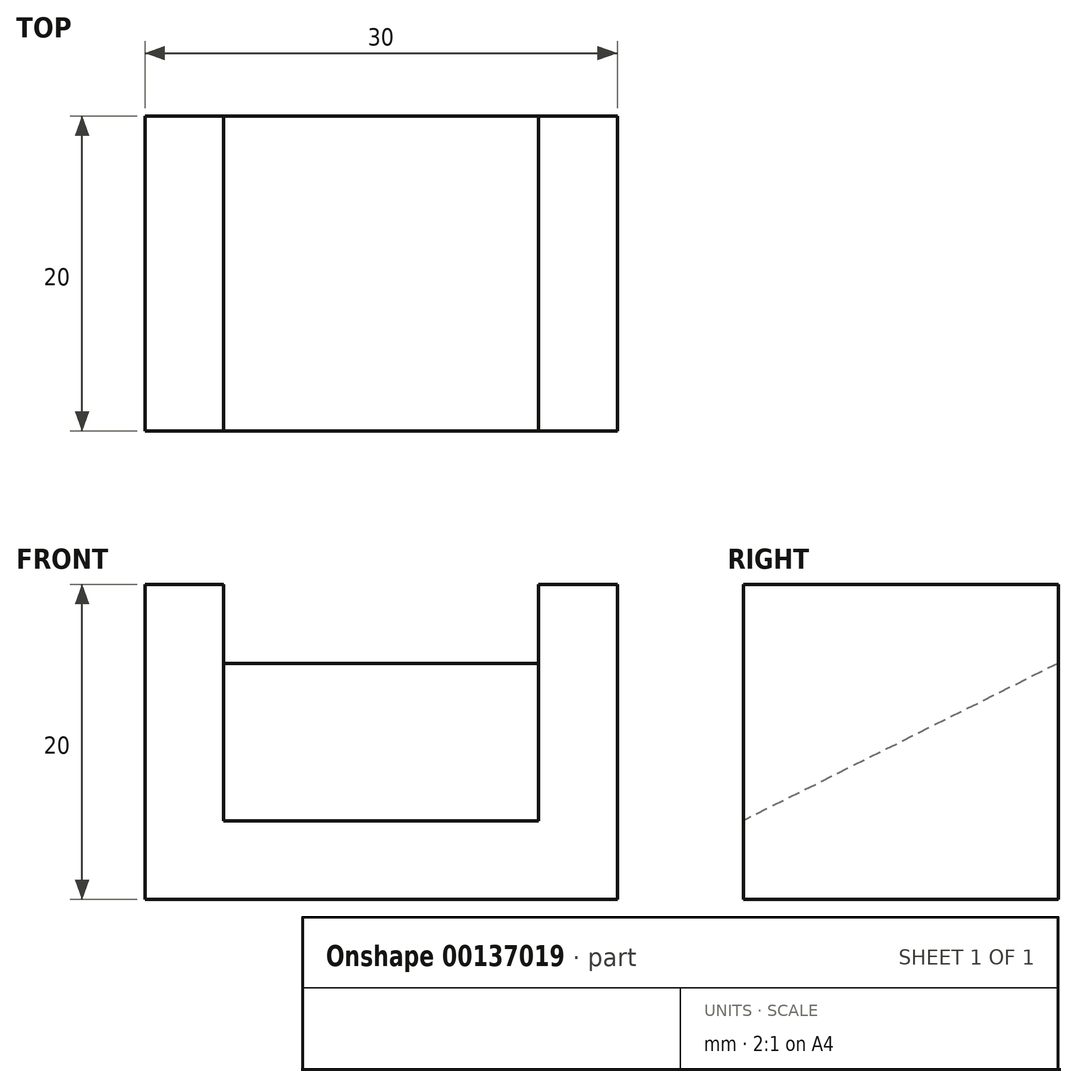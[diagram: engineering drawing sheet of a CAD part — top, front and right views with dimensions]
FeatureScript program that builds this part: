
annotation { "Feature Type Name" : "Feature", "Feature Type Description" : "" }
export const myFeature = defineFeature(function(context is Context, id is Id, definition is map)
    precondition{}
    {
        {
            var Q0;
            Q0=qCreatedBy(makeId("Top.planeOp"),FACE);
            var sketch = newSketch(context, id + "F0", { "sketchPlane" : qUnion([Q0])});
            skLineSegment(sketch, "E0.bottom", {"start": v(0, 0) * mm, "end": v(30, 0) * mm});
            skLineSegment(sketch, "E0.top", {"start": v(0, 20) * mm, "end": v(30, 20) * mm});
            skLineSegment(sketch, "E0.left", {"start": v(0, 0) * mm, "end": v(0, 20) * mm});
            skLineSegment(sketch, "E0.right", {"start": v(30, 0) * mm, "end": v(30, 20) * mm});
            skSolve(sketch);
        }
        {
            var Q0;
            Q0 = qSketchRegion(id + "F0", true);
            extrude(context, id + "F1", {"entities" : qUnion([Q0]), "depth" : 20 * mm});
        }
        {
            var Q0;
            Q0=makeQuery(id+"F1.opExtrude","SWEPT_FACE",FACE,{"disambiguationData":[OSD([sQuery(id+"F0.wireOp",EDGE,"E0.left")])]});
            var sketch = newSketch(context, id + "F2", { "sketchPlane" : qUnion([Q0])});
            skLineSegment(sketch, "E1", {"start": v(-20, 20) * mm, "end": v(-20, 15) * mm});
            skLineSegment(sketch, "E2", {"start": v(-20, 15) * mm, "end": v(0, 5) * mm});
            skLineSegment(sketch, "E3", {"start": v(0, 5) * mm, "end": v(0, 20) * mm});
            skLineSegment(sketch, "E4", {"start": v(0, 20) * mm, "end": v(-20, 20) * mm});
            skSolve(sketch);
        }
        {
            var Q0;
            Q0 = qSketchRegion(id + "F2", true);
            extrude(context, id + "F3", {"entities" : qUnion([Q0]), "operationType" : NewBodyOperationType.REMOVE, "oppositeDirection" : true, "depth" : 25 * mm, "hasSecondDirection" : true, "secondDirectionOppositeDirection" : true, "secondDirectionDepth" : 5 * mm});
        }
    });
